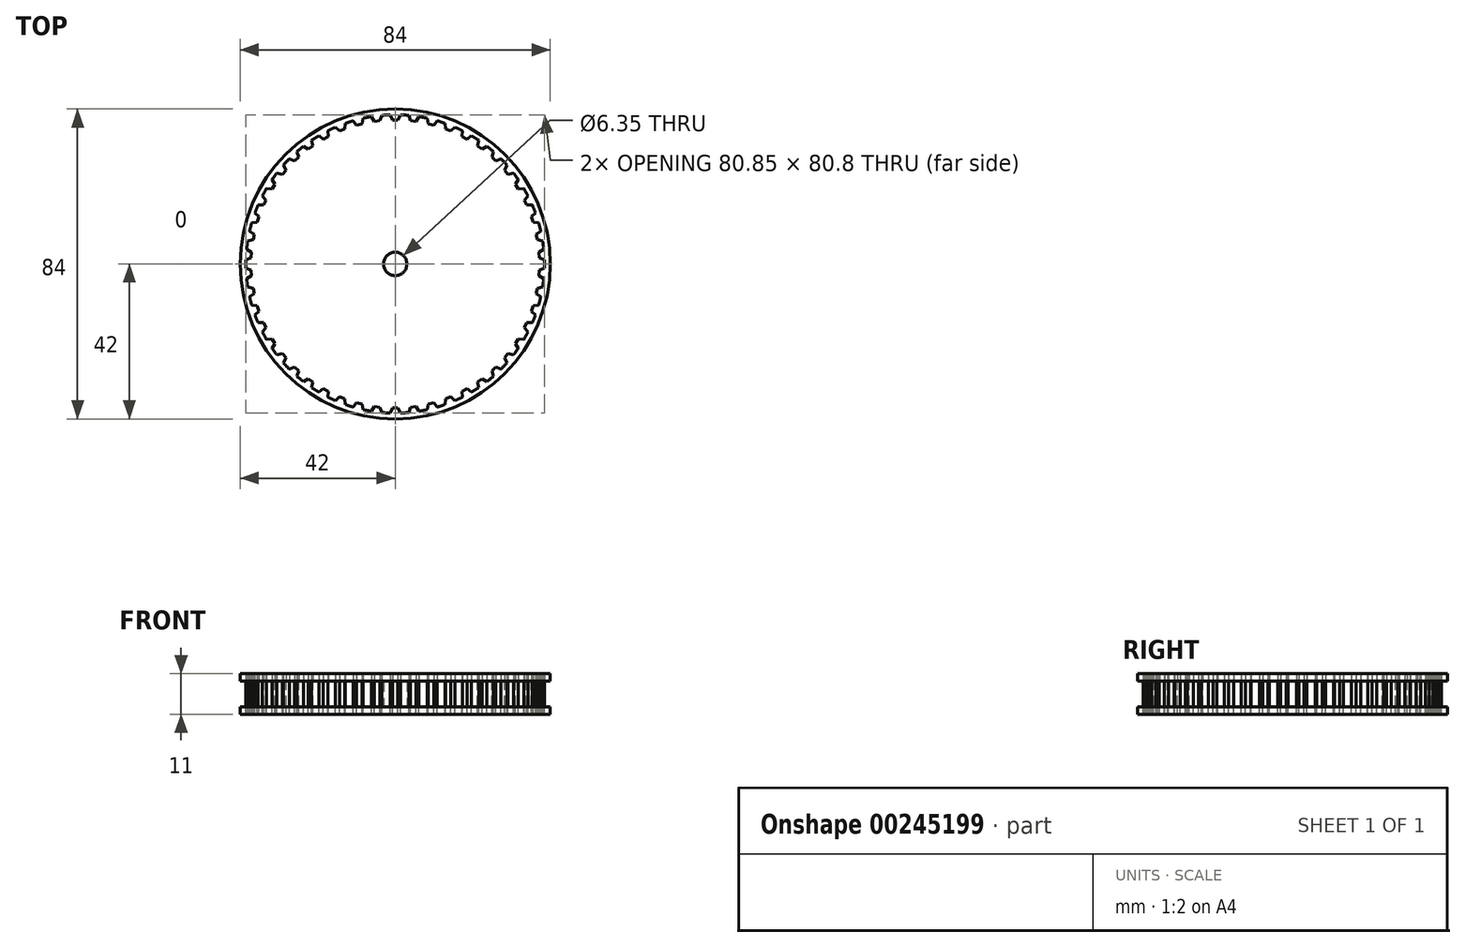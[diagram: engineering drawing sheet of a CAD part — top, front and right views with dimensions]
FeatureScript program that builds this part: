
annotation { "Feature Type Name" : "Feature", "Feature Type Description" : "" }
export const myFeature = defineFeature(function(context is Context, id is Id, definition is map)
    precondition{}
    {
        {
            var Q0;
            Q0=qCreatedBy(makeId("Top.planeOp"),FACE);
            var sketch = newSketch(context, id + "F0", { "sketchPlane" : qUnion([Q0])});
            skCircle(sketch, "E0", {"center": v(0, 0) * mm, "radius": 40.43 * mm});
            skSolve(sketch);
        }
        {
            var Q0;
            Q0=makeQuery(id+"F0.imprint","IMPRINT",FACE,{"disambiguationData":[TD([[makeQuery(id+"F0.imprint","IMPRINT",EDGE,{"derivedFrom":sQuery(id+"F0.wireOp",EDGE,"E0")}),1.0]])]});
            extrude(context, id + "F1", {"entities" : qUnion([Q0]), "endBound" : BoundingType.SYMMETRIC, "depth" : 7 * mm, "hasSecondDirection" : true, "secondDirectionOppositeDirection" : true, "secondDirectionDepth" : 25.4 * mm});
        }
        {
            var Q0;
            Q0=qCreatedBy(makeId("Top.planeOp"),FACE);
            var sketch = newSketch(context, id + "F2", { "sketchPlane" : qUnion([Q0])});
            skArc(sketch, "E1.0", {"start": v(1.4, 40.4) * mm, "mid": v(0, 40.43) * mm, "end": v(-1.4, 40.4) * mm, "construction": true});
            skLineSegment(sketch, "E2", {"start": v(0, 40.43) * mm, "end": v(0, 39.03) * mm, "construction": true});
            skLineSegment(sketch, "E3", {"start": v(-0.75, 39.03) * mm, "end": v(0.75, 39.03) * mm});
            skPoint(sketch, "E4", {"position": v(-1.4, 40.4) * mm});
            skPoint(sketch, "E5", {"position": v(1.4, 40.4) * mm});
            skLineSegment(sketch, "E6", {"start": v(-1.4, 40.4) * mm, "end": v(-0.75, 39.03) * mm});
            skLineSegment(sketch, "E7", {"start": v(1.4, 40.4) * mm, "end": v(0.75, 39.03) * mm});
            skCircle(sketch, "E8.0.0", {"center": v(0, 0) * mm, "radius": 40.43 * mm});
            skSolve(sketch);
        }
        {
            var Q0;
            Q0=makeQuery(id+"F2.imprint","IMPRINT",FACE,{"disambiguationData":[TD([[makeQuery(id+"F2.imprint","IMPRINT",EDGE,{"derivedFrom":sQuery(id+"F2.wireOp",EDGE,"E3")}),1.0]])]});
            extrude(context, id + "F3", {"entities" : qUnion([Q0]), "endBound" : BoundingType.SYMMETRIC, "oppositeDirection" : true, "depth" : 7 * mm});
        }
        {
            var Q0;
            Q0=qCreatedBy(makeId("Right.planeOp"),FACE);
            var sketch = newSketch(context, id + "F4", { "sketchPlane" : qUnion([Q0])});
            skLineSegment(sketch, "E9", {"start": v(0, 22.74) * mm, "end": v(0, -22.84) * mm, "construction": true});
            skSolve(sketch);
        }
        {
            var Q0;
            Q0=makeQuery(id+"F3.opExtrude","SWEPT_BODY",BODY,{"disambiguationData":[OSD([sQuery(id+"F2.wireOp",EDGE,"E3"),sQuery(id+"F2.wireOp",EDGE,"E6"),sQuery(id+"F2.wireOp",EDGE,"E7"),sQuery(id+"F2.wireOp",EDGE,"E8.0.0")])]});
            var Q1;
            Q1=sQuery(id+"F4.wireOp",EDGE,"E9");
            circularPattern(context, id + "F5", {"operationType" : NewBodyOperationType.REMOVE, "entities" : qUnion([Q0]), "axis" : qUnion([Q1]), "angle" : 360 * degree, "instanceCount" : 50, "equalSpace" : true});
        }
        {
            var Q0;
            Q0=makeQuery(id+"F1.opExtrude","CAP_FACE",FACE,{"disambiguationData":[OSD([sQuery(id+"F0.wireOp",EDGE,"E0")])],"isStart":true});
            var sketch = newSketch(context, id + "F6", { "sketchPlane" : qUnion([Q0])});
            skPoint(sketch, "E10.0", {"position": v(0, 0) * mm});
            skCircle(sketch, "E11", {"center": v(0, 0) * mm, "radius": 42 * mm});
            skSolve(sketch);
        }
        {
            var Q0;
            {var subQ10=makeQuery(id+"F3.opExtrude","CAP_EDGE",EDGE,{"disambiguationData":[OSD([sQuery(id+"F2.wireOp",EDGE,"E3")])],"isStart":false});Q0=makeQuery(id+"F6.imprint","IMPRINT",FACE,{"disambiguationData":[TD([[makeQuery(id+"F6.imprint","IMPRINT",EDGE,{"derivedFrom":makeQuery(id+"F5.boolean.opBoolean","COPY",EDGE,{"derivedFrom":subQ10})}),1.0]])]});}
            var Q1;
            Q1=makeQuery(id+"F6.imprint","IMPRINT",FACE,{"disambiguationData":[TD([[makeQuery(id+"F6.imprint","IMPRINT",EDGE,{"derivedFrom":sQuery(id+"F6.wireOp",EDGE,"E11")}),1.0]])]});
            extrude(context, id + "F7", {"entities" : qUnion([Q0, Q1]), "operationType" : NewBodyOperationType.ADD, "depth" : 2 * mm});
        }
        {
            var Q0;
            Q0=makeQuery(id+"F1.opExtrude","CAP_FACE",FACE,{"disambiguationData":[OSD([sQuery(id+"F0.wireOp",EDGE,"E0")])],"isStart":false});
            var sketch = newSketch(context, id + "F8", { "sketchPlane" : qUnion([Q0])});
            skPoint(sketch, "E12.0", {"position": v(0, 0) * mm});
            skCircle(sketch, "E13", {"center": v(0, 0) * mm, "radius": 42 * mm});
            skSolve(sketch);
        }
        {
            var Q0;
            {var subQ10=makeQuery(id+"F3.opExtrude","CAP_EDGE",EDGE,{"disambiguationData":[OSD([sQuery(id+"F2.wireOp",EDGE,"E3")])],"isStart":true});Q0=makeQuery(id+"F8.imprint","IMPRINT",FACE,{"disambiguationData":[TD([[makeQuery(id+"F8.imprint","IMPRINT",EDGE,{"derivedFrom":makeQuery(id+"F5.boolean.opBoolean","COPY",EDGE,{"derivedFrom":subQ10})}),-1.0]])]});}
            var Q1;
            Q1=makeQuery(id+"F8.imprint","IMPRINT",FACE,{"disambiguationData":[TD([[makeQuery(id+"F8.imprint","IMPRINT",EDGE,{"derivedFrom":sQuery(id+"F8.wireOp",EDGE,"E13")}),1.0]])]});
            extrude(context, id + "F9", {"entities" : qUnion([Q0, Q1]), "operationType" : NewBodyOperationType.ADD, "depth" : 2 * mm});
        }
        {
            var Q0;
            Q0=makeQuery(id+"F7.opExtrude","CAP_FACE",FACE,{"disambiguationData":[OSD([sQuery(id+"F6.wireOp",EDGE,"E11")])],"isStart":false});
            var sketch = newSketch(context, id + "F10", { "sketchPlane" : qUnion([Q0])});
            skPoint(sketch, "E14.0", {"position": v(0, 0) * mm});
            skCircle(sketch, "E15", {"center": v(0, 0) * mm, "radius": 3.18 * mm});
            skSolve(sketch);
        }
        {
            var Q0;
            Q0=makeQuery(id+"F10.imprint","IMPRINT",FACE,{"disambiguationData":[TD([[makeQuery(id+"F10.imprint","IMPRINT",EDGE,{"derivedFrom":sQuery(id+"F10.wireOp",EDGE,"E15")}),1.0]])]});
            extrude(context, id + "F11", {"entities" : qUnion([Q0]), "operationType" : NewBodyOperationType.REMOVE, "oppositeDirection" : true, "depth" : 25 * mm});
        }
    });
